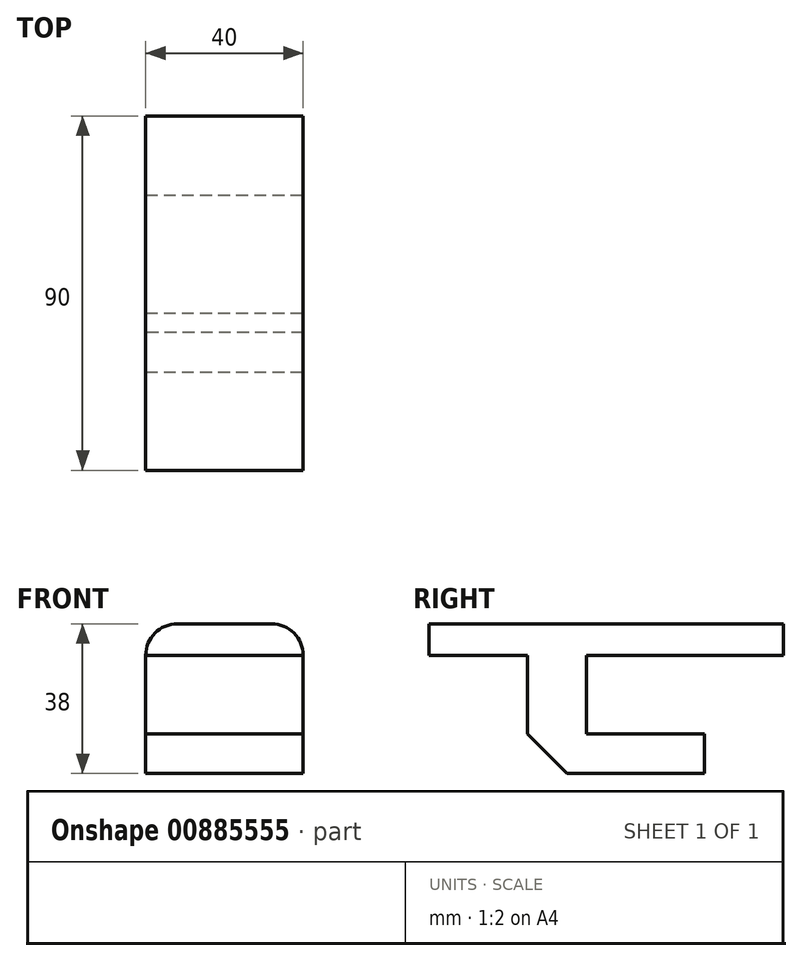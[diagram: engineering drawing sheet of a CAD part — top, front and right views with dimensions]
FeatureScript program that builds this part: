
annotation { "Feature Type Name" : "Feature", "Feature Type Description" : "" }
export const myFeature = defineFeature(function(context is Context, id is Id, definition is map)
    precondition{}
    {
        {
            var Q0;
            Q0=qCreatedBy(makeId("Top.planeOp"),FACE);
            var sketch = newSketch(context, id + "F0", { "sketchPlane" : qUnion([Q0])});
            skLineSegment(sketch, "E0.bottom", {"start": v(-40, -37.9) * mm, "end": v(0, -37.9) * mm});
            skLineSegment(sketch, "E0.top", {"start": v(-40, 52.1) * mm, "end": v(0, 52.1) * mm});
            skLineSegment(sketch, "E0.left", {"start": v(-40, -37.9) * mm, "end": v(-40, 52.1) * mm});
            skLineSegment(sketch, "E0.right", {"start": v(0, -37.9) * mm, "end": v(0, 52.1) * mm});
            skSolve(sketch);
        }
        {
            var Q0;
            Q0 = qSketchRegion(id + "F0", true);
            extrude(context, id + "F1", {"entities" : qUnion([Q0]), "depth" : 8 * mm, "offsetDistance" : 25 * mm});
        }
        {
            var Q0;
            Q0=makeQuery(id+"F1.opExtrude","CAP_FACE",FACE,{"disambiguationData":[OSD([sQuery(id+"F0.wireOp",EDGE,"E0.bottom"),sQuery(id+"F0.wireOp",EDGE,"E0.top"),sQuery(id+"F0.wireOp",EDGE,"E0.left"),sQuery(id+"F0.wireOp",EDGE,"E0.right")])],"isStart":true});
            var sketch = newSketch(context, id + "F2", { "sketchPlane" : qUnion([Q0])});
            skLineSegment(sketch, "E1.bottom", {"start": v(-40, 37.9) * mm, "end": v(0, 37.9) * mm});
            skLineSegment(sketch, "E1.top", {"start": v(-40, -2.1) * mm, "end": v(0, -2.1) * mm});
            skLineSegment(sketch, "E1.left", {"start": v(-40, 37.9) * mm, "end": v(-40, -2.1) * mm});
            skLineSegment(sketch, "E1.right", {"start": v(0, 37.9) * mm, "end": v(0, -2.1) * mm});
            skLineSegment(sketch, "E2.top", {"start": v(-40, 12.9) * mm, "end": v(0, 12.9) * mm});
            skLineSegment(sketch, "E2.left", {"start": v(-40, -2.1) * mm, "end": v(-40, 12.9) * mm});
            skLineSegment(sketch, "E2.right", {"start": v(0, -2.1) * mm, "end": v(0, 12.9) * mm});
            skSolve(sketch);
        }
        {
            var Q0;
            {var subQ0=sQuery(id+"F2.wireOp",EDGE,"E1.top");Q0=makeQuery(id+"F2.imprint","IMPRINT",FACE,{"disambiguationData":[TD([[makeQuery(id+"F2.imprint","IMPRINT",EDGE,{"derivedFrom":subQ0}),1.0]])]});}
            extrude(context, id + "F3", {"entities" : qUnion([Q0]), "operationType" : NewBodyOperationType.ADD, "depth" : 30 * mm, "offsetDistance" : 25 * mm});
        }
        {
            var Q0;
            Q0=makeQuery(id+"F3.opExtrude","SWEPT_FACE",FACE,{"disambiguationData":[OSD([sQuery(id+"F2.wireOp",EDGE,"E1.top")])]});
            var sketch = newSketch(context, id + "F4", { "sketchPlane" : qUnion([Q0])});
            skLineSegment(sketch, "E3.bottom", {"start": v(0, -30) * mm, "end": v(40, -30) * mm});
            skLineSegment(sketch, "E3.top", {"start": v(0, -20) * mm, "end": v(40, -20) * mm});
            skLineSegment(sketch, "E3.left", {"start": v(0, -30) * mm, "end": v(0, -20) * mm});
            skLineSegment(sketch, "E3.right", {"start": v(40, -30) * mm, "end": v(40, -20) * mm});
            skSolve(sketch);
        }
        {
            var Q0;
            Q0 = qSketchRegion(id + "F4", true);
            extrude(context, id + "F5", {"entities" : qUnion([Q0]), "operationType" : NewBodyOperationType.ADD, "depth" : 30 * mm, "offsetDistance" : 25 * mm});
        }
        {
            var Q0;
            Q0=makeQuery(id+"F1.opExtrude","CAP_EDGE",EDGE,{"disambiguationData":[OSD([sQuery(id+"F0.wireOp",EDGE,"E0.right")])],"isStart":false});
            var Q1;
            Q1=makeQuery(id+"F1.opExtrude","CAP_EDGE",EDGE,{"disambiguationData":[OSD([sQuery(id+"F0.wireOp",EDGE,"E0.left")])],"isStart":false});
            fillet(context, id + "F6", {"entities" : qUnion([Q0, Q1]), "radius" : 8 * mm, "tangentPropagation" : true, "allowEdgeOverflow" : false});
        }
        {
            var Q0;
            Q0=makeQuery(id+"F3.opExtrude","CAP_EDGE",EDGE,{"disambiguationData":[OSD([sQuery(id+"F2.wireOp",EDGE,"E2.top")])],"isStart":false});
            chamfer(context, id + "F7", {"entities" : qUnion([Q0]), "chamferType" : ChamferType.TWO_OFFSETS, "width1" : 10 * mm, "oppositeDirection" : true, "width2" : 10 * mm, "tangentPropagation" : true});
        }
    });
